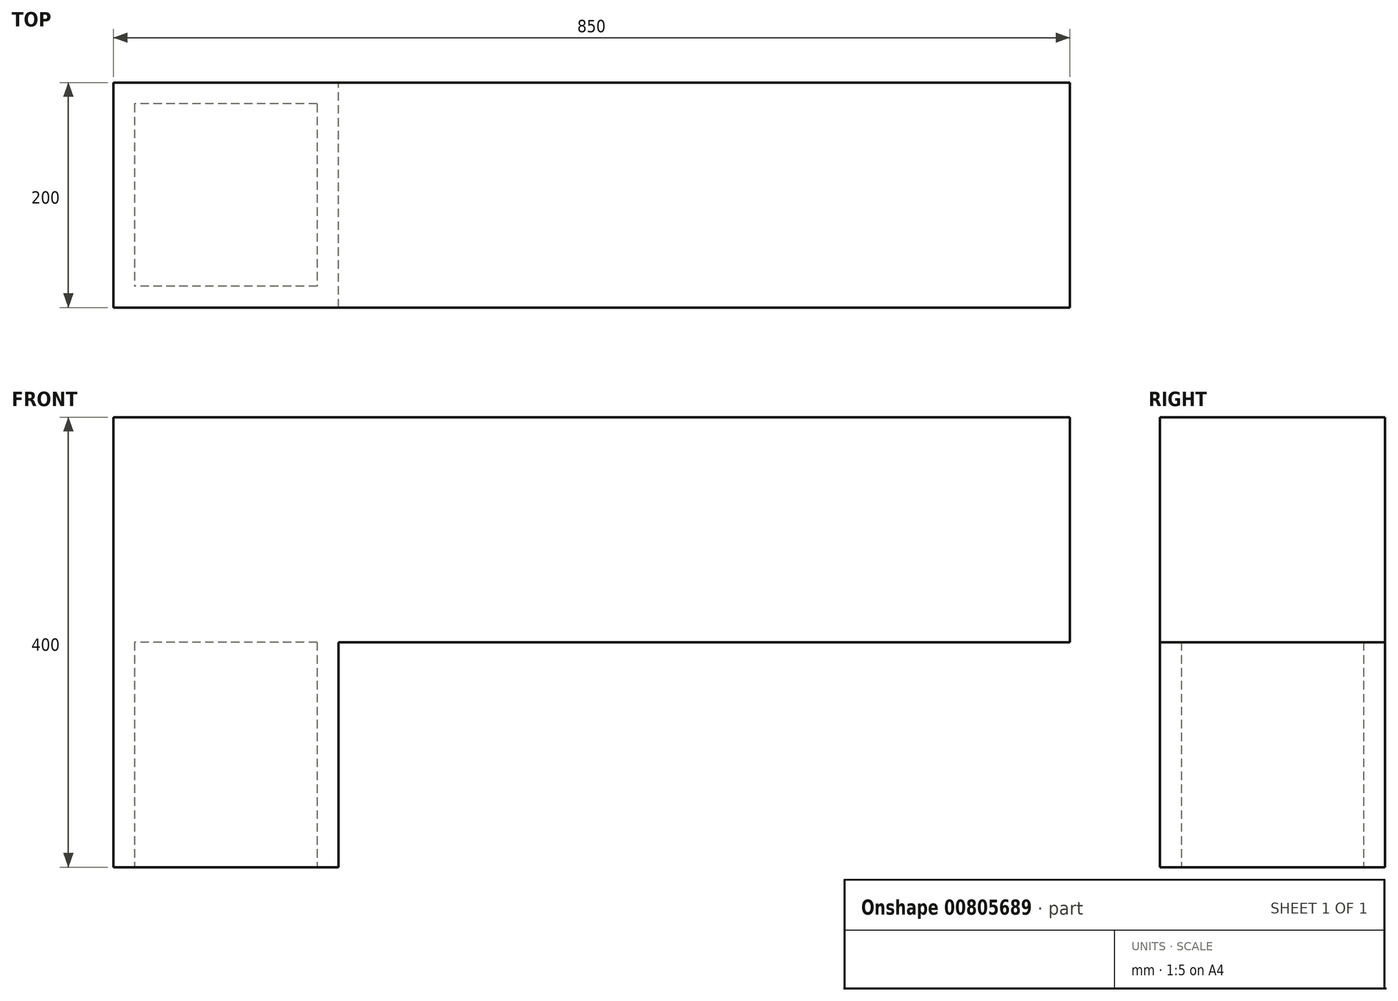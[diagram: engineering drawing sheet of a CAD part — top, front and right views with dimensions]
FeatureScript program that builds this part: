
annotation { "Feature Type Name" : "Feature", "Feature Type Description" : "" }
export const myFeature = defineFeature(function(context is Context, id is Id, definition is map)
    precondition{}
    {
        {
            var Q0;
            Q0=qCreatedBy(makeId("Top.planeOp"),FACE);
            var sketch = newSketch(context, id + "F0", { "sketchPlane" : qUnion([Q0])});
            skLineSegment(sketch, "E0.bottom", {"start": v(100, 100) * mm, "end": v(-100, 100) * mm});
            skLineSegment(sketch, "E0.top", {"start": v(100, -100) * mm, "end": v(-100, -100) * mm});
            skLineSegment(sketch, "E0.left", {"start": v(100, 100) * mm, "end": v(100, -100) * mm});
            skLineSegment(sketch, "E0.right", {"start": v(-100, 100) * mm, "end": v(-100, -100) * mm});
            skPoint(sketch, "E0.middle", {"position": v(0, 0) * mm});
            skLineSegment(sketch, "E1.bottom", {"start": v(81.1, 81.1) * mm, "end": v(-81.1, 81.1) * mm});
            skLineSegment(sketch, "E1.top", {"start": v(81.1, -81.1) * mm, "end": v(-81.1, -81.1) * mm});
            skLineSegment(sketch, "E1.left", {"start": v(81.1, 81.1) * mm, "end": v(81.1, -81.1) * mm});
            skLineSegment(sketch, "E1.right", {"start": v(-81.1, 81.1) * mm, "end": v(-81.1, -81.1) * mm});
            skSolve(sketch);
        }
        {
            var Q0;
            Q0=makeQuery(id+"F0.imprint","IMPRINT",FACE,{"disambiguationData":[TD([[makeQuery(id+"F0.imprint","IMPRINT",EDGE,{"derivedFrom":sQuery(id+"F0.wireOp",EDGE,"E0.bottom")}),1.0]])]});
            extrude(context, id + "F1", {"entities" : qUnion([Q0]), "depth" : 200 * mm, "offsetDistance" : 25 * mm});
        }
        {
            var Q0;
            Q0=makeQuery(id+"F1.opExtrude","CAP_FACE",FACE,{"disambiguationData":[OSD([sQuery(id+"F0.wireOp",EDGE,"E0.bottom"),sQuery(id+"F0.wireOp",EDGE,"E0.top"),sQuery(id+"F0.wireOp",EDGE,"E0.left"),sQuery(id+"F0.wireOp",EDGE,"E0.right"),sQuery(id+"F0.wireOp",EDGE,"E1.bottom"),sQuery(id+"F0.wireOp",EDGE,"E1.top"),sQuery(id+"F0.wireOp",EDGE,"E1.left"),sQuery(id+"F0.wireOp",EDGE,"E1.right")])],"isStart":false});
            var sketch = newSketch(context, id + "F2", { "sketchPlane" : qUnion([Q0])});
            skLineSegment(sketch, "E2.bottom", {"start": v(-100, -100) * mm, "end": v(100, -100) * mm});
            skLineSegment(sketch, "E2.top", {"start": v(-100, 100) * mm, "end": v(100, 100) * mm});
            skLineSegment(sketch, "E2.left", {"start": v(-100, -100) * mm, "end": v(-100, 100) * mm});
            skLineSegment(sketch, "E2.right", {"start": v(100, -100) * mm, "end": v(100, 100) * mm});
            skSolve(sketch);
        }
        {
            var Q0;
            Q0 = qSketchRegion(id + "F2", true);
            extrude(context, id + "F3", {"entities" : qUnion([Q0]), "operationType" : NewBodyOperationType.ADD, "depth" : 200 * mm, "offsetDistance" : 25 * mm});
        }
        {
            var Q0;
            Q0=makeQuery(id+"F3.boolean.opBoolean","MERGE",FACE,{"derivedFrom":[makeQuery(id+"F1.opExtrude","SWEPT_FACE",FACE,{"disambiguationData":[OSD([sQuery(id+"F0.wireOp",EDGE,"E0.left")])]}),makeQuery(id+"F3.opExtrude","SWEPT_FACE",FACE,{"disambiguationData":[OSD([sQuery(id+"F2.wireOp",EDGE,"E2.right")])]})]});
            var sketch = newSketch(context, id + "F4", { "sketchPlane" : qUnion([Q0])});
            skLineSegment(sketch, "E3.bottom", {"start": v(-100, 400) * mm, "end": v(100, 400) * mm});
            skLineSegment(sketch, "E3.top", {"start": v(-100, 200) * mm, "end": v(100, 200) * mm});
            skLineSegment(sketch, "E3.left", {"start": v(-100, 400) * mm, "end": v(-100, 200) * mm});
            skLineSegment(sketch, "E3.right", {"start": v(100, 400) * mm, "end": v(100, 200) * mm});
            skSolve(sketch);
        }
        {
            var Q0;
            Q0 = qSketchRegion(id + "F4", true);
            extrude(context, id + "F5", {"entities" : qUnion([Q0]), "operationType" : NewBodyOperationType.ADD, "depth" : 650 * mm, "offsetDistance" : 25 * mm});
        }
    });
